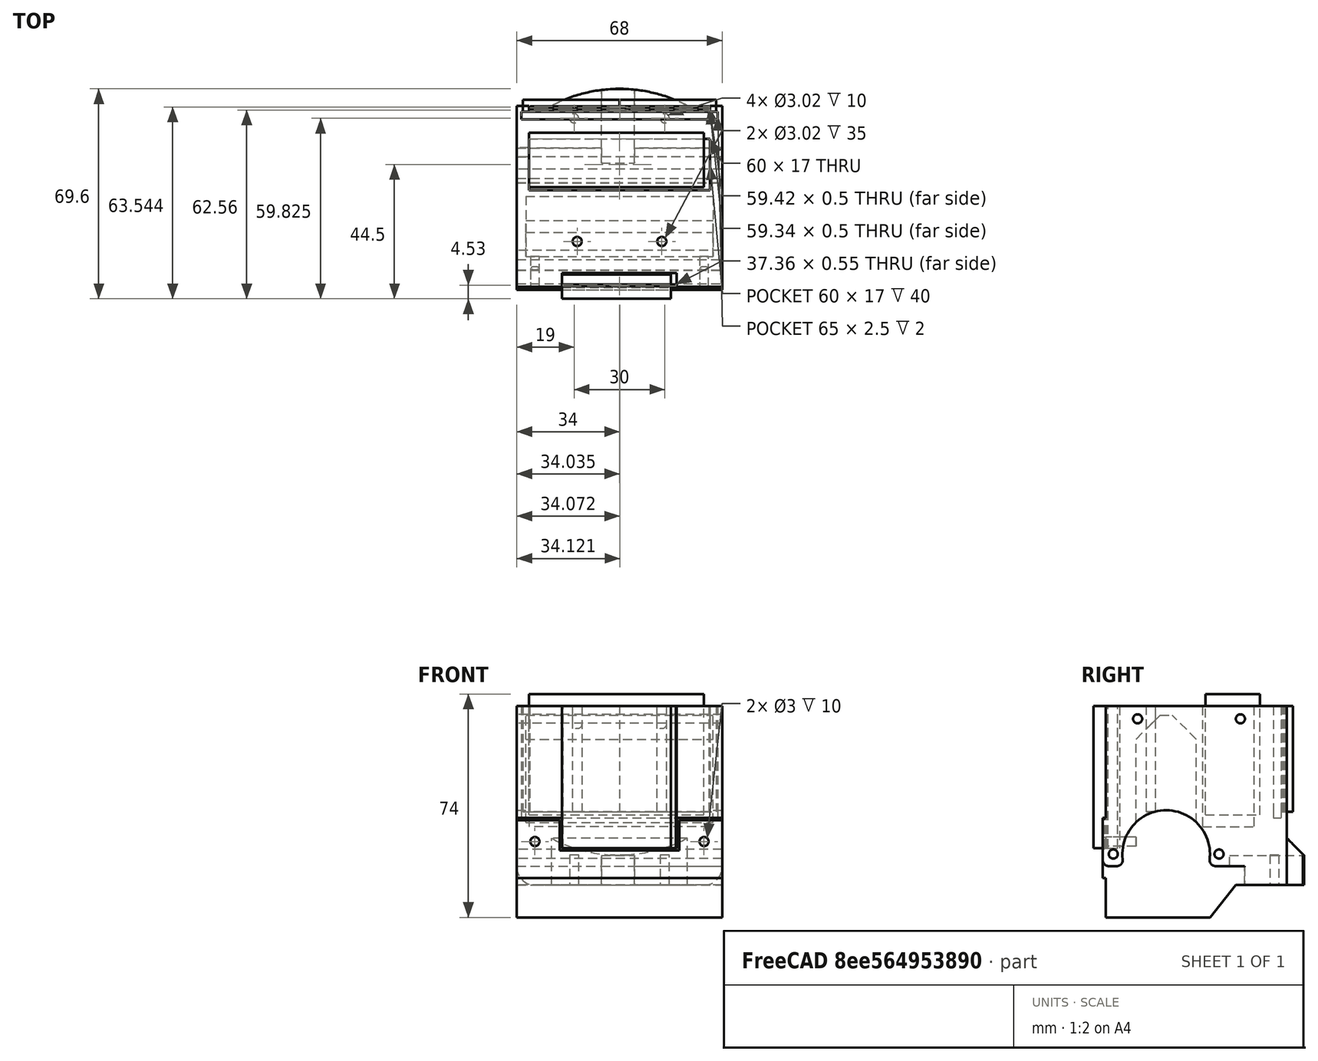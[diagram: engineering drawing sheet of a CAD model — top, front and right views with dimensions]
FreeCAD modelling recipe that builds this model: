
FCSTD DOCUMENT  (FreeCAD 0.17R13541 (Git))
Label: roboLaracha
License: All rights reserved
LicenseURL: http://en.wikipedia.org/wiki/All_rights_reserved
objects: Sketcher::SketchObject×13, PartDesign::Pocket×9, Mesh::Feature×8, Part::Box×8, PartDesign::Pad×4, Part::Fillet×3, Part::Chamfer×2, Part::MultiFuse×2, Part::Cylinder×1, PartDesign::FeatureBase×1, PartDesign::Chamfer×1, PartDesign::ShapeBinder×1, PartDesign::Body×1, Part::Cut×1
note: 60 computed .brp shape members not serialized (recipe doc carries the construction recipe); baked Part::Feature solids carry a one-line shape summary decoded from their .brp

FEATURE [Mesh::Feature] _8BYJ_48  label="28BYJ-48"
  Placement = pos=(-31,103,-1) rot=(0,0,1;3.14159rad)
FEATURE [Mesh::Feature] _8BYJ_049  label="28BYJ-049"
  Placement = pos=(99,-61,-1) rot=(0,0,1;0rad)
FEATURE [Part::Box] Box  label="Cube"
  AttacherType = Attacher::AttachEngine3D
  Height = 70
  Length = 68
  Placement = pos=(0,-2,0) rot=(0,0,1;0rad)
  Width = 60
FEATURE [Part::Box] Box001  label="pilas"
  AttacherType = Attacher::AttachEngine3D
  Height = 40
  Length = 58
  Placement = pos=(4,33,34) rot=(0,0,1;0rad)
  Width = 18
FEATURE [Part::Box] Box002  label="puente"
  AttacherType = Attacher::AttachEngine3D
  Height = 4
  Length = 32
  Placement = pos=(2,58,70) rot=(-1,0,0;1.5708rad)
  Width = 35
FEATURE [Part::Box] Box003  label="puente001"
  AttacherType = Attacher::AttachEngine3D
  Height = 4
  Length = 32
  Placement = pos=(34,58,70) rot=(-1,0,0;1.5708rad)
  Width = 35
FEATURE [Part::Box] Box004  label="Protoboard"
  AttacherType = Attacher::AttachEngine3D
  Height = 47
  Length = 36
  Placement = pos=(15,-4,23) rot=(0,0,1;0rad)
  Width = 8
FEATURE [Mesh::Feature] Arduino_Nano
  Placement = pos=(34,-2,48) rot=(0,-0.707107,0.707107;3.14159rad)
FEATURE [Mesh::Feature] HC_SR04  label="HC-SR04"
  Placement = pos=(55,11,105) rot=(0,0.707107,-0.707107;3.14159rad)
FEATURE [Mesh::Feature] Wheel_72mm
  Placement = pos=(-8,20,28) rot=(0,-1,0;1.5708rad)
FEATURE [Part::Cylinder] Cylinder  label="motores_resta"
  Angle = 360
  AttacherType = Attacher::AttachEngine3D
  Height = 70
  Placement = pos=(-1,20,21) rot=(0.57735,0.57735,0.57735;2.0944rad)
  Radius = 14.5
FEATURE [Part::Box] Box005  label="motores2"
  AttacherType = Attacher::AttachEngine3D
  Height = 19
  Length = 70
  Placement = pos=(-1,-1,-2) rot=(0,0,1;0rad)
  Width = 47
FEATURE [Part::Box] Box006  label="motores003"
  AttacherType = Attacher::AttachEngine3D
  Height = 37
  Length = 62
  Placement = pos=(3,10,30) rot=(0,0,1;0rad)
  Width = 20
FEATURE [Mesh::Feature] BallCaster_14_5mm  label="BallCaster_14.5mm"
  Placement = pos=(34,56,10) rot=(0,1,0;3.14159rad)
FEATURE [Mesh::Feature] SR04Holderv1_1  label="SR04Holderv1-1"
  Placement = pos=(34,8,85) rot=(-0.57735,0.57735,0.57735;2.0944rad)
FEATURE [PartDesign::FeatureBase] BaseFeature
  BaseFeature = -> Box
FEATURE [Sketcher::SketchObject] Sketch
  ExternalGeometry = -> [BaseFeature]
  MapMode = 5
  Placement = pos=(0,0,70) rot=(0,0,1;0rad)
  Support = -> [BaseFeature]
  sketch-geometry (11):
    g0: LineSegment StartX=1.5 StartY=55.5 StartZ=0 EndX=66.5 EndY=55.5 EndZ=0
    g1: LineSegment StartX=66.5 StartY=55.5 StartZ=0 EndX=66.5 EndY=58 EndZ=0
    g2: LineSegment StartX=66.5 StartY=58 StartZ=0 EndX=64 EndY=58 EndZ=0
    g3: LineSegment StartX=64 StartY=58 StartZ=0 EndX=64 EndY=62.7452 EndZ=0
    g4: LineSegment StartX=64 StartY=62.7452 StartZ=0 EndX=4 EndY=62.7452 EndZ=0
    g5: LineSegment StartX=4 StartY=62.7452 StartZ=0 EndX=4 EndY=58 EndZ=0
    g6: LineSegment StartX=4 StartY=58 StartZ=0 EndX=1.5 EndY=58 EndZ=0
    g7: LineSegment StartX=1.5 StartY=58 StartZ=0 EndX=1.5 EndY=55.5 EndZ=0
    g8: LineSegment [constr] StartX=20 StartY=15 StartZ=0 EndX=48 EndY=15 EndZ=0
    g9: Circle CenterX=20 CenterY=15 CenterZ=0 NormalX=0 NormalY=0 NormalZ=1 AngleXU=0 Radius=1.51
    g10: Circle CenterX=48 CenterY=15 CenterZ=0 NormalX=0 NormalY=0 NormalZ=1 AngleXU=0 Radius=1.51
  constraints (31):
    c: Horizontal(g0)
    c: Coincident(g0,g1)
    c: Vertical(g1)
    c: Coincident(g1,g2)
    c: Coincident(g2,g3)
    c: Coincident(g3,g4)
    c: Horizontal(g4)
    c: Coincident(g4,g5)
    c: Coincident(g5,g6)
    c: Horizontal(g6)
    c: Coincident(g6,g7)
    c: Coincident(g7,g0)
    c: Vertical(g7)
    c: Vertical(g5)
    c: Equal(g6,g2)
    c: Vertical(g3)
    c: DistanceX(g0,g0) = 65
    c: DistanceX(g-3,g6) = 1.5
    c: Horizontal(g2)
    c: DistanceY(g1,g-3) = 2
    c: DistanceY(g1,g1) = 2.5
    c: Horizontal(g8)
    c: Coincident(g9,g8)
    c: Coincident(g10,g8)
    c: Radius(g10) = 1.51
    c: Equal(g10,g9)
    c: DistanceX(g8,g8) = 28
    c: DistanceX(g8,g-3) = 20
    c: DistanceY(g8) = 15
    c: Equal(g1,g7)
    c: DistanceX(g2,g1) = 2.5
FEATURE [PartDesign::Pocket] Pocket
  BaseFeature = -> BaseFeature
  Length = 35
  Length2 = 100
  Profile = -> Sketch
  Type = 0
FEATURE [Sketcher::SketchObject] Sketch001
  ExternalGeometry = -> [Pocket]
  MapMode = 5
  Placement = pos=(0,0,35) rot=(0,0,1;0rad)
  Support = -> [Pocket]
  sketch-geometry (4):
    g0: LineSegment StartX=1.5 StartY=58 StartZ=0 EndX=66.5 EndY=58 EndZ=0
    g1: LineSegment StartX=66.5 StartY=58 StartZ=0 EndX=66.5 EndY=55.5 EndZ=0
    g2: LineSegment StartX=1.5 StartY=55.5 StartZ=0 EndX=1.5 EndY=58 EndZ=0
    g3: LineSegment StartX=66.5 StartY=55.5 StartZ=0 EndX=1.5 EndY=55.5 EndZ=0
  constraints (10):
    c: Coincident(g0,g1)
    c: Horizontal(g0)
    c: Vertical(g1)
    c: Coincident(g0,g-4)
    c: Coincident(g2,g0)
    c: Vertical(g2)
    c: Coincident(g1,g-3)
    c: Coincident(g3,g1)
    c: Coincident(g3,g2)
    c: Horizontal(g3)
FEATURE [PartDesign::Pocket] Pocket001
  BaseFeature = -> Pocket
  Length = 2
  Length2 = 100
  Profile = -> Sketch001
  Type = 0
FEATURE [Sketcher::SketchObject] Sketch002
  MapMode = 5
  Placement = pos=(0,0,70) rot=(0,0,1;0rad)
  Support = -> [Pocket001]
  sketch-geometry (4):
    g0: LineSegment StartX=4 StartY=49 StartZ=0 EndX=64 EndY=49 EndZ=0
    g1: LineSegment StartX=64 StartY=49 StartZ=0 EndX=64 EndY=32 EndZ=0
    g2: LineSegment StartX=64 StartY=32 StartZ=0 EndX=4 EndY=32 EndZ=0
    g3: LineSegment StartX=4 StartY=32 StartZ=0 EndX=4 EndY=49 EndZ=0
  constraints (12):
    c: Coincident(g0,g1)
    c: Coincident(g1,g2)
    c: Coincident(g2,g3)
    c: Coincident(g3,g0)
    c: Horizontal(g0)
    c: Horizontal(g2)
    c: Vertical(g1)
    c: Vertical(g3)
    c: DistanceY(g1,g1) = 17
    c: DistanceX(g0,g0) = 60
    c: DistanceX(g2) = 4
    c: DistanceY(g2) = 32
FEATURE [PartDesign::Pocket] Pocket002
  BaseFeature = -> Pocket001
  Length = 40
  Length2 = 100
  Profile = -> Sketch002
  Type = 0
FEATURE [Sketcher::SketchObject] Sketch003
  MapMode = 5
  Placement = pos=(0,0,70) rot=(0,0,1;0rad)
  Support = -> [Pocket002]
  sketch-geometry (4):
    g0: LineSegment StartX=15 StartY=-4.86895 StartZ=0 EndX=53 EndY=-4.86895 EndZ=0
    g1: LineSegment StartX=53 StartY=-4.86895 StartZ=0 EndX=53 EndY=4.5447 EndZ=0
    g2: LineSegment StartX=53 StartY=4.5447 StartZ=0 EndX=15 EndY=4.5447 EndZ=0
    g3: LineSegment StartX=15 StartY=4.5447 StartZ=0 EndX=15 EndY=-4.86895 EndZ=0
  constraints (10):
    c: Coincident(g0,g1)
    c: Coincident(g1,g2)
    c: Coincident(g2,g3)
    c: Coincident(g3,g0)
    c: Horizontal(g0)
    c: Horizontal(g2)
    c: Vertical(g1)
    c: Vertical(g3)
    c: DistanceX(g2,g2) = 38
    c: DistanceX(g-1,g0) = 15
FEATURE [PartDesign::Pocket] Pocket003
  BaseFeature = -> Pocket002
  Length = 47
  Length2 = 100
  Profile = -> Sketch003
  Type = 0
FEATURE [Sketcher::SketchObject] Sketch004
  MapMode = 5
  Placement = pos=(0,0,0) rot=(0.57735,-0.57735,-0.57735;2.0944rad)
  Support = -> [Pocket003]
  sketch-geometry (3):
    g0: LineSegment [constr] StartX=-2.5 StartY=21 StartZ=0 EndX=-37.5 EndY=21 EndZ=0
    g1: Circle CenterX=-37.5 CenterY=21 CenterZ=0 NormalX=0 NormalY=0 NormalZ=1 AngleXU=0 Radius=1.51
    g2: Circle CenterX=-2.5 CenterY=21 CenterZ=0 NormalX=0 NormalY=0 NormalZ=1 AngleXU=0 Radius=1.51
  constraints (8):
    c: Horizontal(g0)
    c: DistanceX(g0,g0) = 35
    c: Coincident(g1,g0)
    c: Coincident(g2,g0)
    c: Radius(g2) = 1.51
    c: Equal(g2,g1)
    c: DistanceX(g0) = -2.5
    c: DistanceY(g0) = 21
FEATURE [PartDesign::Pocket] Pocket004
  BaseFeature = -> Pocket003
  Length = 5
  Length2 = 100
  Profile = -> Sketch004
  Type = 1
FEATURE [Part::Chamfer] Chamfer  label="Chamfer_motores"
  Base = -> Box006
  Edges = 2 edges r=8: [Edge10,Edge12]
FEATURE [Sketcher::SketchObject] Sketch005
  MapMode = 5
  Placement = pos=(68,0,0) rot=(0.57735,0.57735,0.57735;2.0944rad)
  Support = -> [Pocket004]
  sketch-geometry (4):
    g0: LineSegment StartX=25.567 StartY=-11.1911 StartZ=0 EndX=76.1355 EndY=-11.1911 EndZ=0
    g1: LineSegment StartX=76.1355 StartY=-11.1911 StartZ=0 EndX=76.1355 EndY=10.701 EndZ=0
    g2: LineSegment StartX=76.1355 StartY=10.701 StartZ=0 EndX=43.0797 EndY=10.701 EndZ=0
    g3: LineSegment StartX=43.0797 StartY=10.701 StartZ=0 EndX=25.567 EndY=-11.1911 EndZ=0
  constraints (7):
    c: Horizontal(g0)
    c: Coincident(g0,g1)
    c: Vertical(g1)
    c: Coincident(g1,g2)
    c: Horizontal(g2)
    c: Coincident(g2,g3)
    c: Coincident(g3,g0)
FEATURE [PartDesign::Pocket] Pocket005
  BaseFeature = -> Pocket004
  Length = 5
  Length2 = 100
  Profile = -> Sketch005
  Type = 1
FEATURE [Sketcher::SketchObject] Sketch006
  ExternalGeometry = -> [Pocket005]
  MapMode = 5
  Placement = pos=(0,0,10.701) rot=(1,0,0;3.14159rad)
  Support = -> [Pocket005]
  sketch-geometry (3):
    g0: LineSegment [constr] StartX=19 StartY=-55.8251 StartZ=0 EndX=49 EndY=-55.8251 EndZ=0
    g1: Circle CenterX=19 CenterY=-55.8251 CenterZ=0 NormalX=0 NormalY=0 NormalZ=1 AngleXU=0 Radius=1.51
    g2: Circle CenterX=49 CenterY=-55.8251 CenterZ=0 NormalX=0 NormalY=0 NormalZ=1 AngleXU=0 Radius=1.51
  constraints (7):
    c: Horizontal(g0)
    c: Coincident(g1,g0)
    c: Coincident(g2,g0)
    c: Radius(g2) = 1.51
    c: Equal(g2,g1)
    c: DistanceX(g0,g0) = 30
    c: DistanceX(g0) = 19
FEATURE [PartDesign::Pocket] Pocket006
  BaseFeature = -> Pocket005
  Length = 10
  Length2 = 100
  Profile = -> Sketch006
  Type = 0
FEATURE [Sketcher::SketchObject] Sketch007
  ExternalGeometry = -> [Pocket006]
  MapMode = 5
  Placement = pos=(0,0,10.701) rot=(1,0,0;3.14159rad)
  Support = -> [Pocket006]
  sketch-geometry (4):
    g0: ArcOfCircle CenterX=34 CenterY=-17.6001 CenterZ=0 NormalX=0 NormalY=0 NormalZ=1 AngleXU=0 Radius=48 StartAngle=4.22451 EndAngle=5.20026
    g1: LineSegment StartX=11.5 StartY=-60 StartZ=0 EndX=13.0614 EndY=-58.5812 EndZ=0
    g2: LineSegment StartX=13.0614 StartY=-58.5812 StartZ=0 EndX=54.8835 EndY=-58.5812 EndZ=0
    g3: LineSegment StartX=54.8835 StartY=-58.5812 StartZ=0 EndX=56.5 EndY=-60 EndZ=0
  constraints (10):
    c: PointOnObject(g0,g-3)
    c: PointOnObject(g0,g-3)
    c: Radius(g0) = 48
    c: DistanceX(g-3,g0) = 11.5
    c: DistanceX(g0,g-3) = 11.5
    c: Coincident(g0,g1)
    c: Coincident(g1,g2)
    c: Horizontal(g2)
    c: Coincident(g2,g3)
    c: Coincident(g3,g0)
FEATURE [PartDesign::Pad] Pad
  BaseFeature = -> Pocket006
  Length = 10
  Length2 = 100
  Profile = -> Sketch007
  Reversed = true
  Type = 0
FEATURE [PartDesign::Chamfer] Chamfer001
  Base = -> Pad [Edge36]
  BaseFeature = -> Pad
  Size = 5.5
FEATURE [Sketcher::SketchObject] Sketch008
  MapMode = 5
  Placement = pos=(0,0,0) rot=(0.57735,-0.57735,-0.57735;2.0944rad)
  Support = -> [Chamfer001]
  sketch-geometry (3):
    g0: LineSegment [constr] StartX=-44.5901 StartY=65.8135 StartZ=0 EndX=-10.5437 EndY=65.8135 EndZ=0
    g1: Circle CenterX=-44.5901 CenterY=65.8135 CenterZ=0 NormalX=0 NormalY=0 NormalZ=1 AngleXU=0 Radius=1.5
    g2: Circle CenterX=-10.5437 CenterY=65.8135 CenterZ=0 NormalX=0 NormalY=0 NormalZ=1 AngleXU=0 Radius=1.5
  constraints (5):
    c: Horizontal(g0)
    c: Coincident(g1,g0)
    c: Coincident(g2,g0)
    c: Radius(g2) = 1.5
    c: Equal(g2,g1)
FEATURE [PartDesign::Pocket] Pocket007
  BaseFeature = -> Chamfer001
  Length = 5
  Length2 = 100
  Profile = -> Sketch008
  Type = 1
FEATURE [Part::MultiFuse] Fusion  label="Fusion_motores"
  Shapes = -> [Chamfer,Cylinder,Box005]
FEATURE [Part::Box] Box007  label="Cube001"
  AttacherType = Attacher::AttachEngine3D
  Height = 10
  Length = 11
  Placement = pos=(28,41,10.5) rot=(0,0,1;0rad)
  Width = 29
FEATURE [Part::MultiFuse] Fusion001
  Shapes = -> [Box007,Fusion]
FEATURE [PartDesign::ShapeBinder] ReferenceChamfer002001
FEATURE [Sketcher::SketchObject] Sketch009
  ExternalGeometry = -> [Pocket007]
  MapMode = 5
  Placement = pos=(0,0,35) rot=(0,0,1;0rad)
  Support = -> [ReferenceChamfer002001]
  sketch-geometry (8):
    g0: LineSegment StartX=4.36195 StartY=59.7945 StartZ=0 EndX=63.782 EndY=59.7945 EndZ=0
    g1: LineSegment StartX=63.782 StartY=59.7945 StartZ=0 EndX=63.782 EndY=59.2945 EndZ=0
    g2: LineSegment StartX=63.782 StartY=59.2945 StartZ=0 EndX=4.36195 EndY=59.2945 EndZ=0
    g3: LineSegment StartX=4.36195 StartY=59.2945 StartZ=0 EndX=4.36195 EndY=59.7945 EndZ=0
    g4: LineSegment StartX=63.7902 StartY=58.3097 StartZ=0 EndX=4.45131 EndY=58.3097 EndZ=0
    g5: LineSegment StartX=4.45131 StartY=58.3097 StartZ=0 EndX=4.45131 EndY=58.8097 EndZ=0
    g6: LineSegment StartX=4.45131 StartY=58.8097 StartZ=0 EndX=63.7902 EndY=58.8097 EndZ=0
    g7: LineSegment StartX=63.7902 StartY=58.8097 StartZ=0 EndX=63.7902 EndY=58.3097 EndZ=0
  constraints (18):
    c: Coincident(g0,g1)
    c: Coincident(g1,g2)
    c: Coincident(g2,g3)
    c: Coincident(g3,g0)
    c: Horizontal(g0)
    c: Horizontal(g2)
    c: Vertical(g1)
    c: Vertical(g3)
    c: Coincident(g4,g5)
    c: Coincident(g5,g6)
    c: Coincident(g6,g7)
    c: Coincident(g7,g4)
    c: Horizontal(g4)
    c: Horizontal(g6)
    c: Vertical(g5)
    c: Vertical(g7)
    c: DistanceY(g7,g7) = 0.5
    c: DistanceY(g1,g1) = 0.5
FEATURE [PartDesign::Pad] Pad001
  BaseFeature = -> Pocket007
  Length = 35
  Length2 = 100
  Profile = -> Sketch009
  Type = 0
FEATURE [Sketcher::SketchObject] Sketch010
  MapMode = 5
  Placement = pos=(0,0,23) rot=(0,0,1;0rad)
  Support = -> [Pad001]
  sketch-geometry (4):
    g0: LineSegment StartX=15.3566 StartY=0.25395 StartZ=0 EndX=52.7135 EndY=0.25395 EndZ=0
    g1: LineSegment StartX=52.7135 StartY=0.25395 StartZ=0 EndX=52.7135 EndY=0.805558 EndZ=0
    g2: LineSegment StartX=52.7135 StartY=0.805558 StartZ=0 EndX=15.3566 EndY=0.805558 EndZ=0
    g3: LineSegment StartX=15.3566 StartY=0.805558 StartZ=0 EndX=15.3566 EndY=0.25395 EndZ=0
  constraints (8):
    c: Coincident(g0,g1)
    c: Coincident(g1,g2)
    c: Coincident(g2,g3)
    c: Coincident(g3,g0)
    c: Horizontal(g0)
    c: Horizontal(g2)
    c: Vertical(g1)
    c: Vertical(g3)
FEATURE [PartDesign::Pad] Pad002
  BaseFeature = -> Pad001
  Length = 47
  Length2 = 100
  Profile = -> Sketch010
  Type = 0
FEATURE [Sketcher::SketchObject] Sketch011
  ExternalGeometry = -> [Pad002]
  MapMode = 5
  Placement = pos=(0,0,0) rot=(1,0,0;1.5708rad)
  Support = -> [Pad002]
  sketch-geometry (3):
    g0: LineSegment [constr] StartX=6 StartY=25.1273 StartZ=0 EndX=62 EndY=25.1273 EndZ=0
    g1: Circle CenterX=6 CenterY=25.1273 CenterZ=0 NormalX=0 NormalY=0 NormalZ=1 AngleXU=0 Radius=1.5
    g2: Circle CenterX=62 CenterY=25.1273 CenterZ=0 NormalX=0 NormalY=0 NormalZ=1 AngleXU=0 Radius=1.5
  constraints (7):
    c: Horizontal(g0)
    c: DistanceX(g-4,g0) = 6
    c: DistanceX(g0,g-3) = 6
    c: Coincident(g1,g0)
    c: Coincident(g2,g0)
    c: Radius(g2) = 1.5
    c: Equal(g2,g1)
FEATURE [PartDesign::Pocket] Pocket008
  BaseFeature = -> Pad002
  Length = 10
  Length2 = 100
  Profile = -> Sketch011
  Type = 0
FEATURE [Sketcher::SketchObject] Sketch012
  ExternalGeometry = -> [Pocket008]
  MapMode = 5
  Placement = pos=(0,0,0) rot=(1,0,0;1.5708rad)
  Support = -> [Pocket008]
  sketch-geometry (10):
    g0: LineSegment StartX=0 StartY=33 StartZ=0 EndX=15 EndY=33 EndZ=0
    g1: LineSegment StartX=15 StartY=33 StartZ=0 EndX=15 EndY=23 EndZ=0
    g2: LineSegment StartX=15 StartY=23 StartZ=0 EndX=53 EndY=23 EndZ=0
    g3: LineSegment StartX=53 StartY=23 StartZ=0 EndX=53 EndY=33 EndZ=0
    g4: LineSegment StartX=53 StartY=33 StartZ=0 EndX=68 EndY=33 EndZ=0
    g5: LineSegment StartX=68 StartY=33 StartZ=0 EndX=68 EndY=13.0223 EndZ=0
    g6: LineSegment StartX=68 StartY=13.0223 StartZ=0 EndX=0 EndY=13.0223 EndZ=0
    g7: LineSegment StartX=0 StartY=13.0223 StartZ=0 EndX=0 EndY=33 EndZ=0
    g8: Circle CenterX=6 CenterY=25.1273 CenterZ=0 NormalX=0 NormalY=0 NormalZ=1 AngleXU=0 Radius=1.51
    g9: Circle CenterX=62 CenterY=25.1273 CenterZ=0 NormalX=0 NormalY=0 NormalZ=1 AngleXU=0 Radius=1.51
  constraints (25):
    c: PointOnObject(g0,g-3)
    c: Horizontal(g0)
    c: Coincident(g0,g1)
    c: Coincident(g1,g-5)
    c: Coincident(g1,g2)
    c: Coincident(g2,g-5)
    c: Coincident(g2,g3)
    c: Coincident(g3,g4)
    c: PointOnObject(g4,g-4)
    c: Horizontal(g4)
    c: Coincident(g4,g5)
    c: PointOnObject(g5,g-4)
    c: Coincident(g5,g6)
    c: PointOnObject(g6,g-3)
    c: Horizontal(g6)
    c: Coincident(g6,g7)
    c: Coincident(g7,g0)
    c: Vertical(g3)
    c: Vertical(g1)
    c: Equal(g1,g3)
    c: DistanceY(g1,g1) = 10
    c: Coincident(g8,g-6)
    c: Coincident(g9,g-7)
    c: Radius(g9) = 1.51
    c: Equal(g9,g8)
FEATURE [PartDesign::Pad] Pad003
  BaseFeature = -> Pocket008
  Length = 1
  Length2 = 100
  Profile = -> Sketch012
  Type = 0
FEATURE [PartDesign::Body] Body
  BaseFeature = -> Box
  Group = -> [BaseFeature,Sketch,Pocket,Sketch001,Pocket001,Sketch002,Pocket002,Sketch003,Pocket003,Sketch004,Pocket004,Sketch005,Pocket005,Sketch006,Pocket006,Sketch007,Pad,Chamfer001,Sketch008,Pocket007,ReferenceChamfer002001,Sketch009,Pad001,Sketch010,Pad002,Sketch011,Pocket008,Sketch012,Pad003]
  Origin = -> Origin
  Tip = -> Pad003
FEATURE [Part::Cut] Cut
  Base = -> Pad003
  Tool = -> Fusion001
FEATURE [Part::Chamfer] Chamfer002
  Base = -> Cut
  Edges = 5 edges r=0.8: [Edge203,Edge204,Edge205,Edge206,Edge207]
FEATURE [Part::Fillet] Fillet
  Base = -> Chamfer002
  Edges = 1 edges r=2: [Edge8]
FEATURE [Part::Fillet] Fillet001
  Base = -> Fillet
  Edges = 2 edges r=2: [Edge63,Edge71]
FEATURE [Part::Fillet] Fillet002
  Base = -> Fillet001
  Edges = 2 edges r=6: [Edge13,Edge99]
FEATURE [Mesh::Feature] Wheel_72mm001
  Placement = pos=(76,20,28) rot=(0,1,0;1.5708rad)
